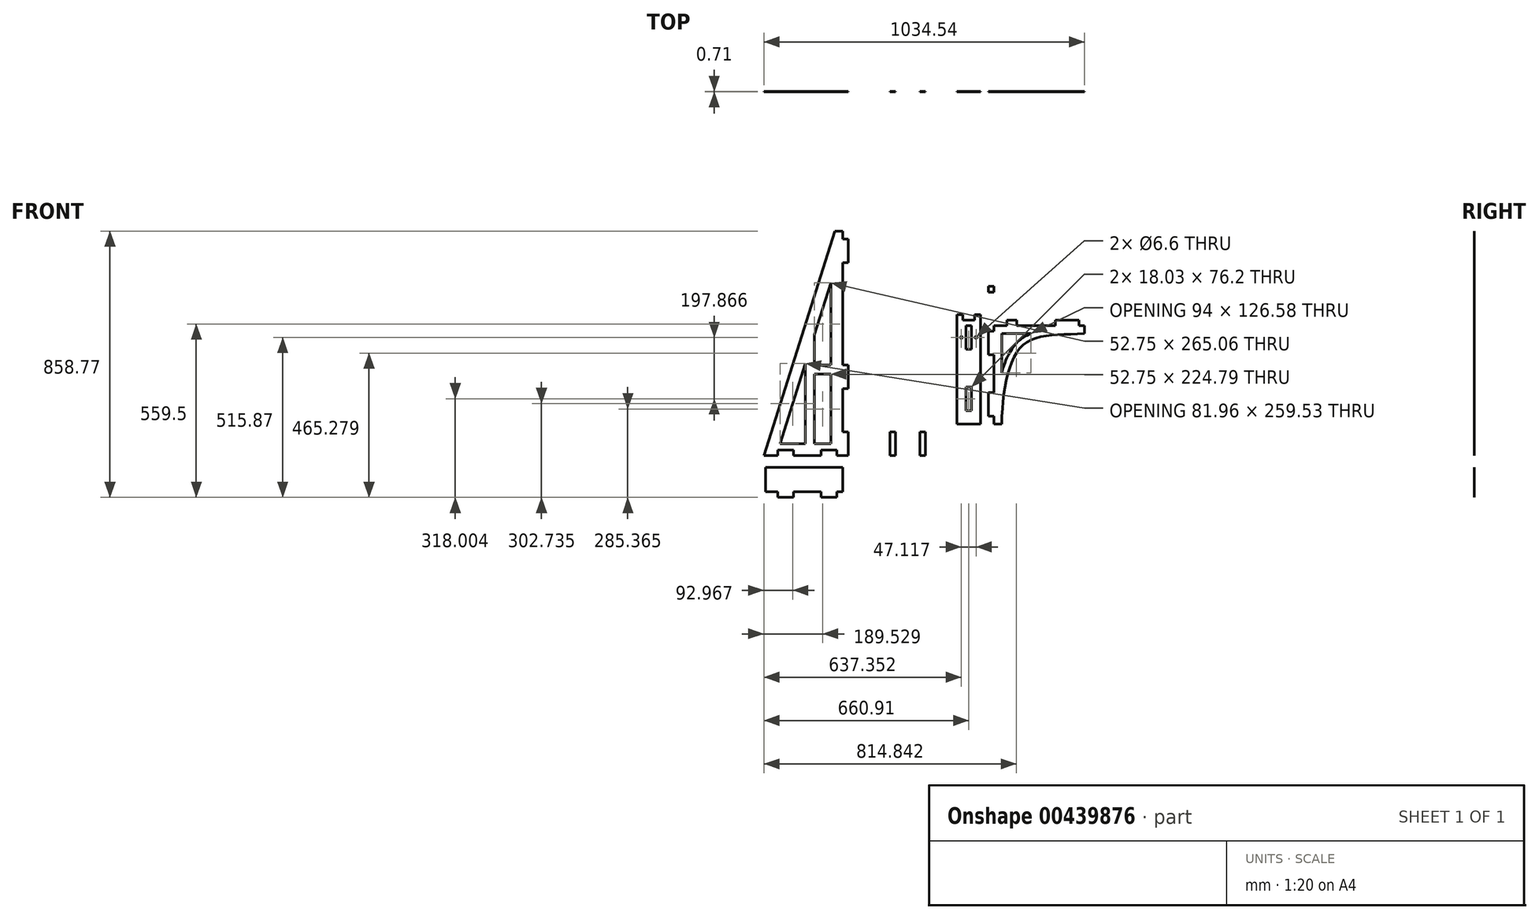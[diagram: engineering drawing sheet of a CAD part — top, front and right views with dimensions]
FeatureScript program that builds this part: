
annotation { "Feature Type Name" : "Feature", "Feature Type Description" : "" }
export const myFeature = defineFeature(function(context is Context, id is Id, definition is map)
    precondition{}
    {
        {
            assignVariable(context, id + "F0", {"name" : "ply34", "anyValue" : .71});
        }
        {
            var Q0;
            Q0=qCreatedBy(makeId("Front.planeOp"),FACE);
            var sketch = newSketch(context, id + "F1", { "sketchPlane" : qUnion([Q0])});
            skLineSegment(sketch, "E0.bottom", {"start": v(-508, 38.1) * mm, "end": v(508, 38.1) * mm});
            skLineSegment(sketch, "E0.top", {"start": v(-508, -38.1) * mm, "end": v(508, -38.1) * mm});
            skLineSegment(sketch, "E0.left", {"start": v(-508, 38.1) * mm, "end": v(-508, -38.1) * mm});
            skLineSegment(sketch, "E0.right", {"start": v(508, 38.1) * mm, "end": v(508, -38.1) * mm});
            skPoint(sketch, "E0.middle", {"position": v(0, 0) * mm});
            skLineSegment(sketch, "E1", {"start": v(0, 0) * mm, "end": v(-152.4, 0) * mm});
            skLineSegment(sketch, "E2", {"start": v(-152.4, 0) * mm, "end": v(0, 0) * mm});
            skLineSegment(sketch, "E3", {"start": v(0, 0) * mm, "end": v(152.4, 0) * mm});
            skArc(sketch, "E4.0.startCap", {"start": v(-152.4, -3.3) * mm, "mid": v(-155.7, 0) * mm, "end": v(-152.4, 3.3) * mm});
            skArc(sketch, "E4.0.endCap", {"start": v(0, 3.3) * mm, "mid": v(3.3, 0) * mm, "end": v(0, -3.3) * mm});
            skLineSegment(sketch, "E4.0.left", {"start": v(-152.4, 3.3) * mm, "end": v(0, 3.3) * mm});
            skLineSegment(sketch, "E4.0.right", {"start": v(-152.4, -3.3) * mm, "end": v(0, -3.3) * mm});
            skArc(sketch, "E4.1.startCap", {"start": v(0, -3.3) * mm, "mid": v(-3.3, 0) * mm, "end": v(0, 3.3) * mm});
            skArc(sketch, "E4.1.endCap", {"start": v(152.4, 3.3) * mm, "mid": v(155.7, 0) * mm, "end": v(152.4, -3.3) * mm});
            skLineSegment(sketch, "E4.1.left", {"start": v(0, 3.3) * mm, "end": v(152.4, 3.3) * mm});
            skLineSegment(sketch, "E4.1.right", {"start": v(0, -3.3) * mm, "end": v(152.4, -3.3) * mm});
            skLineSegment(sketch, "E5.bottom", {"start": v(-292.1, 9.02) * mm, "end": v(-215.9, 9.02) * mm});
            skLineSegment(sketch, "E5.top", {"start": v(-292.1, -9.02) * mm, "end": v(-215.9, -9.02) * mm});
            skLineSegment(sketch, "E5.left", {"start": v(-292.1, 9.02) * mm, "end": v(-292.1, -9.02) * mm});
            skLineSegment(sketch, "E5.right", {"start": v(-215.9, 9.02) * mm, "end": v(-215.9, -9.02) * mm});
            skPoint(sketch, "E5.middle", {"position": v(-254, 0) * mm});
            skLineSegment(sketch, "E6.bottom", {"start": v(-415.93, 9.02) * mm, "end": v(-447.68, 9.02) * mm});
            skLineSegment(sketch, "E6.top", {"start": v(-415.93, -9.02) * mm, "end": v(-447.68, -9.02) * mm});
            skLineSegment(sketch, "E6.left", {"start": v(-415.93, 9.02) * mm, "end": v(-415.93, -9.02) * mm});
            skLineSegment(sketch, "E6.right", {"start": v(-447.68, 9.02) * mm, "end": v(-447.68, -9.02) * mm});
            skPoint(sketch, "E6.middle", {"position": v(-431.8, 0) * mm});
            skPoint(sketch, "E6.middle.positionSnap0", {"position": v(-292.1, 0) * mm});
            skPoint(sketch, "E6.centerSnap0", {"position": v(-292.1, 0) * mm});
            skLineSegment(sketch, "E7.bottom", {"start": v(-508, 38.1) * mm, "end": v(-489.97, 38.1) * mm});
            skLineSegment(sketch, "E7.top", {"start": v(-508, 19.05) * mm, "end": v(-489.97, 19.05) * mm});
            skLineSegment(sketch, "E7.left", {"start": v(-508, 38.1) * mm, "end": v(-508, 19.05) * mm});
            skLineSegment(sketch, "E7.right", {"start": v(-489.97, 38.1) * mm, "end": v(-489.97, 19.05) * mm});
            skLineSegment(sketch, "E8.bottom", {"start": v(-508, -38.1) * mm, "end": v(-489.97, -38.1) * mm});
            skLineSegment(sketch, "E8.top", {"start": v(-508, -19.05) * mm, "end": v(-489.97, -19.05) * mm});
            skLineSegment(sketch, "E8.left", {"start": v(-508, -38.1) * mm, "end": v(-508, -19.05) * mm});
            skLineSegment(sketch, "E8.right", {"start": v(-489.97, -38.1) * mm, "end": v(-489.97, -19.05) * mm});
            skLineSegment(sketch, "E9", {"start": v(-489.97, -88.9) * mm, "end": v(-197.87, -88.9) * mm});
            skLineSegment(sketch, "E10", {"start": v(-197.87, -88.9) * mm, "end": v(-197.87, -114.3) * mm});
            skLineSegment(sketch, "E11", {"start": v(-489.97, -88.9) * mm, "end": v(-489.97, -381) * mm});
            skLineSegment(sketch, "E12", {"start": v(-489.97, -381) * mm, "end": v(-464.57, -381) * mm, "construction": true});
            skFitSpline(sketch, "E13", {"points": [v(-197.87, -114.3) * mm, v(-396.07, -151.38) * mm, v(-464.57, -381) * mm], "startDerivative": vector(-532.47, -33.14) * mm, "endDerivative": vector(-35.57, -553.13) * mm});
            skFitSpline(sketch, "E14.0", {"points": [v(-199.05, -95.29) * mm, v(-209.95, -95.96) * mm, v(-231.35, -96.96) * mm, v(-262.2, -98.06) * mm, v(-291.7, -99.5) * mm, v(-315.11, -101.64) * mm, v(-333.14, -104.34) * mm, v(-346.3, -106.98) * mm, v(-359.07, -110.37) * mm, v(-371.45, -114.64) * mm, v(-383.38, -119.94) * mm, v(-392.88, -125.32) * mm, v(-400.15, -130.26) * mm, v(-404.55, -133.62) * mm, v(-407.97, -136.47) * mm, v(-411.32, -139.43) * mm, v(-415.36, -143.3) * mm, v(-419.95, -148.22) * mm, v(-425.77, -155.12) * mm, v(-432.47, -164.32) * mm, v(-439.67, -176.21) * mm, v(-448.25, -193.08) * mm, v(-457.24, -215.9) * mm, v(-465.75, -245.64) * mm, v(-472.36, -277.33) * mm, v(-477.36, -310.53) * mm, v(-481.06, -344.83) * mm, v(-482.83, -368.1) * mm, v(-483.58, -379.78) * mm]});
            skLineSegment(sketch, "E15.0", {"start": v(-464.57, -114.3) * mm, "end": v(-370.05, -114.3) * mm});
            skLineSegment(sketch, "E15.1", {"start": v(-464.57, -114.3) * mm, "end": v(-464.57, -242.5) * mm});
            skLineSegment(sketch, "E16", {"start": v(-292.1, -88.9) * mm, "end": v(-292.1, -70.87) * mm});
            skLineSegment(sketch, "E17", {"start": v(-292.1, -70.87) * mm, "end": v(-215.9, -70.87) * mm});
            skLineSegment(sketch, "E18", {"start": v(-215.9, -70.87) * mm, "end": v(-215.9, -88.9) * mm});
            skLineSegment(sketch, "E19", {"start": v(-447.68, -88.9) * mm, "end": v(-447.68, -70.87) * mm});
            skLineSegment(sketch, "E20", {"start": v(-447.68, -70.87) * mm, "end": v(-415.93, -70.87) * mm});
            skLineSegment(sketch, "E21", {"start": v(-415.93, -70.87) * mm, "end": v(-415.93, -88.9) * mm});
            skLineSegment(sketch, "E22", {"start": v(-489.97, -381) * mm, "end": v(-508, -381) * mm});
            skLineSegment(sketch, "E23", {"start": v(-508, -381) * mm, "end": v(-508, -304.8) * mm});
            skLineSegment(sketch, "E24", {"start": v(-508, -304.8) * mm, "end": v(-489.97, -304.8) * mm});
            skLineSegment(sketch, "E25.bottom", {"start": v(-533.4, -70.87) * mm, "end": v(-609.6, -70.87) * mm});
            skLineSegment(sketch, "E25.top", {"start": v(-533.4, -406.4) * mm, "end": v(-609.6, -406.4) * mm});
            skLineSegment(sketch, "E25.left", {"start": v(-533.4, -70.87) * mm, "end": v(-533.4, -406.4) * mm});
            skLineSegment(sketch, "E25.right", {"start": v(-609.6, -70.87) * mm, "end": v(-609.6, -406.4) * mm});
            skLineSegment(sketch, "E26", {"start": v(-609.6, -70.87) * mm, "end": v(-609.6, -52.83) * mm});
            skLineSegment(sketch, "E27", {"start": v(-609.6, -52.83) * mm, "end": v(-590.55, -52.83) * mm});
            skLineSegment(sketch, "E28", {"start": v(-590.55, -52.83) * mm, "end": v(-590.55, -70.87) * mm});
            skLineSegment(sketch, "E29", {"start": v(-533.4, -70.87) * mm, "end": v(-533.4, -52.83) * mm});
            skLineSegment(sketch, "E30", {"start": v(-533.4, -52.83) * mm, "end": v(-552.45, -52.83) * mm});
            skLineSegment(sketch, "E31", {"start": v(-552.45, -52.83) * mm, "end": v(-552.45, -70.87) * mm});
            skLineSegment(sketch, "E32.bottom", {"start": v(-562.48, -88.9) * mm, "end": v(-580.52, -88.9) * mm});
            skLineSegment(sketch, "E32.top", {"start": v(-562.48, -165.1) * mm, "end": v(-580.52, -165.1) * mm});
            skLineSegment(sketch, "E32.left", {"start": v(-562.48, -88.9) * mm, "end": v(-562.48, -165.1) * mm});
            skLineSegment(sketch, "E32.right", {"start": v(-580.52, -88.9) * mm, "end": v(-580.52, -165.1) * mm});
            skPoint(sketch, "E32.middle", {"position": v(-571.5, -127) * mm});
            skPoint(sketch, "E32.middle.positionSnap1", {"position": v(-571.5, -70.87) * mm});
            skPoint(sketch, "E32.centerSnap1", {"position": v(-571.5, -70.87) * mm});
            skPoint(sketch, "E33.middle.positionSnap0", {"position": v(-571.5, -406.4) * mm});
            skPoint(sketch, "E33.middle.positionSnap1", {"position": v(-508, -342.9) * mm});
            skPoint(sketch, "E33.centerSnap0", {"position": v(-571.5, -406.4) * mm});
            skPoint(sketch, "E33.centerSnap1", {"position": v(-508, -342.9) * mm});
            skLineSegment(sketch, "E34.top", {"start": v(-489.97, -406.4) * mm, "end": v(-464.57, -406.4) * mm});
            skLineSegment(sketch, "E34.left", {"start": v(-489.97, -381) * mm, "end": v(-489.97, -406.4) * mm});
            skLineSegment(sketch, "E34.right", {"start": v(-464.57, -381) * mm, "end": v(-464.57, -406.4) * mm});
            skLineSegment(sketch, "E35", {"start": v(-580.52, -127) * mm, "end": v(-609.6, -127) * mm, "construction": true});
            skCircle(sketch, "E36", {"center": v(-595.06, -127) * mm, "radius": 3.3 * mm});
            skLineSegment(sketch, "E37", {"start": v(-562.48, -127) * mm, "end": v(-533.4, -127) * mm, "construction": true});
            skCircle(sketch, "E38", {"center": v(-547.94, -127) * mm, "radius": 3.3 * mm});
            skLineSegment(sketch, "E39.bottom", {"start": v(-826, 406.4) * mm, "end": v(-711.2, 406.4) * mm});
            skLineSegment(sketch, "E39.top", {"start": v(-826, -508) * mm, "end": v(-711.2, -508) * mm});
            skLineSegment(sketch, "E39.left", {"start": v(-826, 406.4) * mm, "end": v(-826, -508) * mm});
            skLineSegment(sketch, "E39.right", {"start": v(-711.2, 406.4) * mm, "end": v(-711.2, -508) * mm});
            skLineSegment(sketch, "E40.bottom", {"start": v(-711.2, -508) * mm, "end": v(-729.23, -508) * mm});
            skLineSegment(sketch, "E40.top", {"start": v(-711.2, -431.8) * mm, "end": v(-729.23, -431.8) * mm});
            skLineSegment(sketch, "E40.left", {"start": v(-711.2, -508) * mm, "end": v(-711.2, -431.8) * mm});
            skLineSegment(sketch, "E40.right", {"start": v(-729.23, -508) * mm, "end": v(-729.23, -431.8) * mm});
            skLineSegment(sketch, "E41.bottom", {"start": v(-711.2, 406.4) * mm, "end": v(-729.23, 406.4) * mm, "construction": true});
            skLineSegment(sketch, "E41.top", {"start": v(-711.2, 355.6) * mm, "end": v(-729.23, 355.6) * mm, "construction": true});
            skLineSegment(sketch, "E41.left", {"start": v(-711.2, 406.4) * mm, "end": v(-711.2, 355.6) * mm, "construction": true});
            skLineSegment(sketch, "E41.right", {"start": v(-729.23, 406.4) * mm, "end": v(-729.23, 355.6) * mm, "construction": true});
            skLineSegment(sketch, "E42", {"start": v(-768.6, 406.4) * mm, "end": v(-768.6, -508) * mm, "construction": true});
            skLineSegment(sketch, "E43.MirrorCS", {"start": v(-826, 406.4) * mm, "end": v(-807.97, 406.4) * mm, "construction": true});
            skLineSegment(sketch, "E44.MirrorCS", {"start": v(-826, 406.4) * mm, "end": v(-826, 355.6) * mm, "construction": true});
            skLineSegment(sketch, "E45.MirrorCS", {"start": v(-807.97, 406.4) * mm, "end": v(-807.97, 355.6) * mm, "construction": true});
            skLineSegment(sketch, "E46.MirrorCS", {"start": v(-826, 355.6) * mm, "end": v(-807.97, 355.6) * mm, "construction": true});
            skLineSegment(sketch, "E47.MirrorCS", {"start": v(-807.97, -508) * mm, "end": v(-807.97, -431.8) * mm});
            skLineSegment(sketch, "E48.MirrorCS", {"start": v(-826, -431.8) * mm, "end": v(-807.97, -431.8) * mm});
            skLineSegment(sketch, "E49.MirrorCS", {"start": v(-826, -508) * mm, "end": v(-826, -431.8) * mm});
            skLineSegment(sketch, "E50.MirrorCS", {"start": v(-826, -508) * mm, "end": v(-807.97, -508) * mm});
            skLineSegment(sketch, "E51.bottom", {"start": v(-711.2, -215.9) * mm, "end": v(-729.23, -215.9) * mm});
            skLineSegment(sketch, "E51.top", {"start": v(-711.2, -292.1) * mm, "end": v(-729.23, -292.1) * mm});
            skLineSegment(sketch, "E51.left", {"start": v(-711.2, -215.9) * mm, "end": v(-711.2, -292.1) * mm});
            skLineSegment(sketch, "E51.right", {"start": v(-729.23, -215.9) * mm, "end": v(-729.23, -292.1) * mm});
            skLineSegment(sketch, "E52.bottom", {"start": v(-711.2, 190.5) * mm, "end": v(-729.23, 190.5) * mm});
            skLineSegment(sketch, "E52.top", {"start": v(-711.2, 114.3) * mm, "end": v(-729.23, 114.3) * mm});
            skLineSegment(sketch, "E52.left", {"start": v(-711.2, 190.5) * mm, "end": v(-711.2, 114.3) * mm});
            skLineSegment(sketch, "E52.right", {"start": v(-729.23, 190.5) * mm, "end": v(-729.23, 114.3) * mm});
            skLineSegment(sketch, "E53.MirrorCS", {"start": v(-826, -215.9) * mm, "end": v(-807.97, -215.9) * mm});
            skLineSegment(sketch, "E54.MirrorCS", {"start": v(-826, -292.1) * mm, "end": v(-807.97, -292.1) * mm});
            skLineSegment(sketch, "E55.MirrorCS", {"start": v(-826, 190.5) * mm, "end": v(-807.97, 190.5) * mm});
            skLineSegment(sketch, "E56.MirrorCS", {"start": v(-826, 114.3) * mm, "end": v(-807.97, 114.3) * mm});
            skLineSegment(sketch, "E57.MirrorCS", {"start": v(-807.97, 190.5) * mm, "end": v(-807.97, 114.3) * mm});
            skLineSegment(sketch, "E58.MirrorCS", {"start": v(-826, 190.5) * mm, "end": v(-826, 114.3) * mm});
            skLineSegment(sketch, "E59.MirrorCS", {"start": v(-807.97, -215.9) * mm, "end": v(-807.97, -292.1) * mm});
            skLineSegment(sketch, "E60.MirrorCS", {"start": v(-826, -215.9) * mm, "end": v(-826, -292.1) * mm});
            skLineSegment(sketch, "E61", {"start": v(-595.06, -127) * mm, "end": v(-547.94, -127) * mm, "construction": true});
            skLineSegment(sketch, "E62", {"start": v(-792.16, -50.8) * mm, "end": v(-745.05, -50.8) * mm, "construction": true});
            skPoint(sketch, "E62.startSnap0", {"position": v(-768.6, -50.8) * mm});
            skLineSegment(sketch, "E63", {"start": v(-792.16, 76.2) * mm, "end": v(-792.16, -177.8) * mm, "construction": true});
            skLineSegment(sketch, "E64", {"start": v(-745.05, 76.2) * mm, "end": v(-745.05, -177.8) * mm, "construction": true});
            skArc(sketch, "E65.0.startCap", {"start": v(-795.46, 76.2) * mm, "mid": v(-792.16, 79.5) * mm, "end": v(-788.86, 76.2) * mm});
            skArc(sketch, "E65.0.endCap", {"start": v(-788.86, -177.8) * mm, "mid": v(-792.16, -181.1) * mm, "end": v(-795.46, -177.8) * mm});
            skLineSegment(sketch, "E65.0.left", {"start": v(-788.86, 76.2) * mm, "end": v(-788.86, -177.8) * mm});
            skLineSegment(sketch, "E65.0.right", {"start": v(-795.46, 76.2) * mm, "end": v(-795.46, -177.8) * mm});
            skArc(sketch, "E66.0.startCap", {"start": v(-748.35, 76.2) * mm, "mid": v(-745.05, 79.5) * mm, "end": v(-741.74, 76.2) * mm});
            skArc(sketch, "E66.0.endCap", {"start": v(-741.74, -177.8) * mm, "mid": v(-745.05, -181.1) * mm, "end": v(-748.35, -177.8) * mm});
            skLineSegment(sketch, "E66.0.left", {"start": v(-741.74, 76.2) * mm, "end": v(-741.74, -177.8) * mm});
            skLineSegment(sketch, "E66.0.right", {"start": v(-748.35, 76.2) * mm, "end": v(-748.35, -177.8) * mm});
            skLineSegment(sketch, "E67", {"start": v(-978.4, 215.9) * mm, "end": v(-978.4, -508) * mm});
            skLineSegment(sketch, "E68", {"start": v(-978.4, -508) * mm, "end": v(-1232.4, -508) * mm});
            skLineSegment(sketch, "E69", {"start": v(-1232.4, -508) * mm, "end": v(-1003.8, 215.9) * mm});
            skLineSegment(sketch, "E70", {"start": v(-1003.8, 215.9) * mm, "end": v(-978.4, 215.9) * mm});
            skLineSegment(sketch, "E71", {"start": v(-978.4, 190.5) * mm, "end": v(-960.37, 190.5) * mm});
            skLineSegment(sketch, "E72", {"start": v(-960.37, 190.5) * mm, "end": v(-960.37, 114.3) * mm});
            skLineSegment(sketch, "E73", {"start": v(-960.37, 114.3) * mm, "end": v(-978.4, 114.3) * mm});
            skLineSegment(sketch, "E74", {"start": v(-978.4, -215.9) * mm, "end": v(-960.37, -215.9) * mm});
            skLineSegment(sketch, "E75", {"start": v(-960.37, -215.9) * mm, "end": v(-960.37, -292.1) * mm});
            skLineSegment(sketch, "E76", {"start": v(-960.37, -292.1) * mm, "end": v(-978.4, -292.1) * mm});
            skLineSegment(sketch, "E77", {"start": v(-978.4, -508) * mm, "end": v(-960.37, -508) * mm});
            skLineSegment(sketch, "E78", {"start": v(-960.37, -508) * mm, "end": v(-960.37, -431.8) * mm});
            skLineSegment(sketch, "E79", {"start": v(-960.37, -431.8) * mm, "end": v(-978.4, -431.8) * mm});
            skLineSegment(sketch, "E80.0", {"start": v(-1016.5, 49.16) * mm, "end": v(-1016.5, -215.9) * mm});
            skLineSegment(sketch, "E80.1", {"start": v(-1180.42, -469.9) * mm, "end": v(-1098.46, -210.37) * mm});
            skLineSegment(sketch, "E80.2", {"start": v(-1016.5, -469.9) * mm, "end": v(-1069.25, -469.9) * mm});
            skLineSegment(sketch, "E81", {"start": v(-1098.46, -469.9) * mm, "end": v(-1098.46, -210.37) * mm});
            skLineSegment(sketch, "E82", {"start": v(-1069.25, -469.9) * mm, "end": v(-1069.25, -245.11) * mm});
            skLineSegment(sketch, "E83.trimOffspring", {"start": v(-1069.25, -117.87) * mm, "end": v(-1016.5, 49.16) * mm});
            skLineSegment(sketch, "E84.trimOffspring", {"start": v(-1098.46, -469.9) * mm, "end": v(-1180.42, -469.9) * mm});
            skLineSegment(sketch, "E85", {"start": v(-1016.5, -215.9) * mm, "end": v(-1069.25, -215.9) * mm});
            skLineSegment(sketch, "E86", {"start": v(-1069.25, -245.11) * mm, "end": v(-1016.5, -245.11) * mm});
            skLineSegment(sketch, "E87.trimOffspring", {"start": v(-1016.5, -245.11) * mm, "end": v(-1016.5, -469.9) * mm});
            skLineSegment(sketch, "E88.trimOffspring", {"start": v(-1069.25, -215.9) * mm, "end": v(-1069.25, -117.87) * mm});
            skLineSegment(sketch, "E89", {"start": v(-997.46, -508) * mm, "end": v(-997.46, -489.97) * mm});
            skLineSegment(sketch, "E90", {"start": v(-997.46, -489.97) * mm, "end": v(-1048.26, -489.97) * mm});
            skLineSegment(sketch, "E91", {"start": v(-1048.26, -489.97) * mm, "end": v(-1048.26, -508) * mm});
            skLineSegment(sketch, "E92", {"start": v(-1048.26, -508) * mm, "end": v(-997.46, -508) * mm});
            skLineSegment(sketch, "E93.bottom", {"start": v(-1137.16, -508) * mm, "end": v(-1187.96, -508) * mm});
            skLineSegment(sketch, "E93.top", {"start": v(-1137.16, -489.97) * mm, "end": v(-1187.96, -489.97) * mm});
            skLineSegment(sketch, "E93.left", {"start": v(-1137.16, -508) * mm, "end": v(-1137.16, -489.97) * mm});
            skLineSegment(sketch, "E93.right", {"start": v(-1187.96, -508) * mm, "end": v(-1187.96, -489.97) * mm});
            skLineSegment(sketch, "E94", {"start": v(-1226.71, -489.97) * mm, "end": v(-1226.71, -508) * mm, "construction": true});
            skLineSegment(sketch, "E95.bottom", {"start": v(-1226.71, -546.1) * mm, "end": v(-978.4, -546.1) * mm});
            skLineSegment(sketch, "E95.top", {"start": v(-1226.71, -624.84) * mm, "end": v(-978.4, -624.84) * mm});
            skLineSegment(sketch, "E95.left", {"start": v(-1226.71, -546.1) * mm, "end": v(-1226.71, -624.84) * mm});
            skLineSegment(sketch, "E95.right", {"start": v(-978.4, -546.1) * mm, "end": v(-978.4, -624.84) * mm});
            skLineSegment(sketch, "E96", {"start": v(-807.97, -469.9) * mm, "end": v(-729.23, -469.9) * mm, "construction": true});
            skLineSegment(sketch, "E97.bottom", {"start": v(-1187.96, -546.1) * mm, "end": v(-1137.16, -546.1) * mm});
            skLineSegment(sketch, "E97.top", {"start": v(-1187.96, -528.07) * mm, "end": v(-1137.16, -528.07) * mm});
            skLineSegment(sketch, "E97.left", {"start": v(-1187.96, -546.1) * mm, "end": v(-1187.96, -528.07) * mm});
            skLineSegment(sketch, "E97.right", {"start": v(-1137.16, -546.1) * mm, "end": v(-1137.16, -528.07) * mm});
            skLineSegment(sketch, "E98.bottom", {"start": v(-997.46, -546.1) * mm, "end": v(-1048.26, -546.1) * mm});
            skLineSegment(sketch, "E98.top", {"start": v(-997.46, -528.07) * mm, "end": v(-1048.26, -528.07) * mm});
            skLineSegment(sketch, "E98.left", {"start": v(-997.46, -546.1) * mm, "end": v(-997.46, -528.07) * mm});
            skLineSegment(sketch, "E98.right", {"start": v(-1048.26, -546.1) * mm, "end": v(-1048.26, -528.07) * mm});
            skLineSegment(sketch, "E99", {"start": v(-1226.71, -585.47) * mm, "end": v(-978.4, -585.47) * mm, "construction": true});
            skLineSegment(sketch, "E100.MirrorCS", {"start": v(-1187.96, -642.87) * mm, "end": v(-1137.16, -642.87) * mm});
            skLineSegment(sketch, "E101.MirrorCS", {"start": v(-1187.96, -624.84) * mm, "end": v(-1137.16, -624.84) * mm});
            skLineSegment(sketch, "E102.MirrorCS", {"start": v(-1187.96, -624.84) * mm, "end": v(-1187.96, -642.87) * mm});
            skLineSegment(sketch, "E103.MirrorCS", {"start": v(-997.46, -642.87) * mm, "end": v(-1048.26, -642.87) * mm});
            skLineSegment(sketch, "E104.MirrorCS", {"start": v(-1137.16, -624.84) * mm, "end": v(-1137.16, -642.87) * mm});
            skLineSegment(sketch, "E105.MirrorCS", {"start": v(-997.46, -624.84) * mm, "end": v(-997.46, -642.87) * mm});
            skLineSegment(sketch, "E106.MirrorCS", {"start": v(-1048.26, -624.84) * mm, "end": v(-1048.26, -642.87) * mm});
            skLineSegment(sketch, "E107.MirrorCS", {"start": v(-997.46, -624.84) * mm, "end": v(-1048.26, -624.84) * mm});
            skLineSegment(sketch, "E108.bottom", {"start": v(-489.97, -106.93) * mm, "end": v(-508, -106.93) * mm});
            skLineSegment(sketch, "E108.top", {"start": v(-489.97, -183.13) * mm, "end": v(-508, -183.13) * mm});
            skLineSegment(sketch, "E108.left", {"start": v(-489.97, -106.93) * mm, "end": v(-489.97, -183.13) * mm});
            skLineSegment(sketch, "E108.right", {"start": v(-508, -106.93) * mm, "end": v(-508, -183.13) * mm});
            skLineSegment(sketch, "E109.bottom", {"start": v(-562.48, -362.97) * mm, "end": v(-580.52, -362.97) * mm});
            skLineSegment(sketch, "E109.top", {"start": v(-562.48, -286.77) * mm, "end": v(-580.52, -286.77) * mm});
            skLineSegment(sketch, "E109.left", {"start": v(-562.48, -362.97) * mm, "end": v(-562.48, -286.77) * mm});
            skLineSegment(sketch, "E109.right", {"start": v(-580.52, -362.97) * mm, "end": v(-580.52, -286.77) * mm});
            skPoint(sketch, "E109.middle", {"position": v(-571.5, -324.87) * mm});
            skLineSegment(sketch, "E110", {"start": v(-508, -183.13) * mm, "end": v(-508, -304.8) * mm, "construction": true});
            skLineSegment(sketch, "E111", {"start": v(-562.48, -165.1) * mm, "end": v(-562.48, -286.77) * mm, "construction": true});
            skLineSegment(sketch, "E112", {"start": v(-768.6, 406.4) * mm, "end": v(-768.6, 381) * mm});
            skArc(sketch, "E113.0.startCap", {"start": v(-771.9, 406.4) * mm, "mid": v(-768.6, 409.7) * mm, "end": v(-765.3, 406.4) * mm});
            skArc(sketch, "E113.0.endCap", {"start": v(-765.3, 381) * mm, "mid": v(-768.6, 377.7) * mm, "end": v(-771.9, 381) * mm});
            skLineSegment(sketch, "E113.0.left", {"start": v(-765.3, 406.4) * mm, "end": v(-765.3, 381) * mm});
            skLineSegment(sketch, "E113.0.right", {"start": v(-771.9, 406.4) * mm, "end": v(-771.9, 381) * mm});
            skLineSegment(sketch, "E114", {"start": v(508, 0) * mm, "end": v(469.9, 0) * mm, "construction": true});
            skLineSegment(sketch, "E115", {"start": v(469.9, 15.87) * mm, "end": v(469.9, -15.87) * mm, "construction": true});
            skCircle(sketch, "E116", {"center": v(469.9, 15.87) * mm, "radius": 9.53 * mm});
            skCircle(sketch, "E117", {"center": v(469.9, -15.87) * mm, "radius": 9.53 * mm});
            skSolve(sketch);
        }
        {
            var Q0;
            {var subQ14=sQuery(id+"F1.wireOp",EDGE,"E69");Q0=makeQuery(id+"F1.imprint","IMPRINT",FACE,{"disambiguationData":[TD([[makeQuery(id+"F1.imprint","IMPRINT",EDGE,{"derivedFrom":subQ14}),-1.0]])]});}
            var Q1;
            {var subQ0=sQuery(id+"F1.wireOp",EDGE,"E71");Q1=makeQuery(id+"F1.imprint","IMPRINT",FACE,{"disambiguationData":[TD([[makeQuery(id+"F1.imprint","IMPRINT",EDGE,{"derivedFrom":subQ0}),-1.0]])]});}
            var Q2;
            {var subQ0=sQuery(id+"F1.wireOp",EDGE,"E74");Q2=makeQuery(id+"F1.imprint","IMPRINT",FACE,{"disambiguationData":[TD([[makeQuery(id+"F1.imprint","IMPRINT",EDGE,{"derivedFrom":subQ0}),-1.0]])]});}
            var Q3;
            {var subQ0=sQuery(id+"F1.wireOp",EDGE,"E77");Q3=makeQuery(id+"F1.imprint","IMPRINT",FACE,{"disambiguationData":[TD([[makeQuery(id+"F1.imprint","IMPRINT",EDGE,{"derivedFrom":subQ0}),1.0]])]});}
            var Q4;
            Q4=makeQuery(id+"F1.imprint","IMPRINT",FACE,{"disambiguationData":[TD([[makeQuery(id+"F1.imprint","IMPRINT",EDGE,{"derivedFrom":sQuery(id+"F1.wireOp",EDGE,"E98.bottom")}),-1.0]])]});
            var Q5;
            Q5=makeQuery(id+"F1.imprint","IMPRINT",FACE,{"disambiguationData":[TD([[makeQuery(id+"F1.imprint","IMPRINT",EDGE,{"derivedFrom":sQuery(id+"F1.wireOp",EDGE,"E97.bottom")}),1.0]])]});
            var Q6;
            {var subQ2=sQuery(id+"F1.wireOp",EDGE,"E95.left");Q6=makeQuery(id+"F1.imprint","IMPRINT",FACE,{"disambiguationData":[TD([[makeQuery(id+"F1.imprint","IMPRINT",EDGE,{"derivedFrom":subQ2}),1.0]])]});}
            var Q7;
            Q7=makeQuery(id+"F1.imprint","IMPRINT",FACE,{"disambiguationData":[TD([[makeQuery(id+"F1.imprint","IMPRINT",EDGE,{"derivedFrom":sQuery(id+"F1.wireOp",EDGE,"E103.MirrorCS")}),-1.0]])]});
            var Q8;
            Q8=makeQuery(id+"F1.imprint","IMPRINT",FACE,{"disambiguationData":[TD([[makeQuery(id+"F1.imprint","IMPRINT",EDGE,{"derivedFrom":sQuery(id+"F1.wireOp",EDGE,"E0.bottom")}),-1.0]])]});
            var Q9;
            {var subQ6=sQuery(id+"F1.wireOp",EDGE,"E10");Q9=makeQuery(id+"F1.imprint","IMPRINT",FACE,{"disambiguationData":[TD([[makeQuery(id+"F1.imprint","IMPRINT",EDGE,{"derivedFrom":subQ6}),-1.0]])]});}
            var Q10;
            {var subQ0=sQuery(id+"F1.wireOp",EDGE,"E16");Q10=makeQuery(id+"F1.imprint","IMPRINT",FACE,{"disambiguationData":[TD([[makeQuery(id+"F1.imprint","IMPRINT",EDGE,{"derivedFrom":subQ0}),-1.0]])]});}
            var Q11;
            {var subQ0=sQuery(id+"F1.wireOp",EDGE,"E19");Q11=makeQuery(id+"F1.imprint","IMPRINT",FACE,{"disambiguationData":[TD([[makeQuery(id+"F1.imprint","IMPRINT",EDGE,{"derivedFrom":subQ0}),-1.0]])]});}
            var Q12;
            {var subQ0=sQuery(id+"F1.wireOp",EDGE,"XXwvfhwP-Kl7B-pzMR-Daqk-7tzTg0mTjpYv");Q12=makeQuery(id+"F1.imprint","IMPRINT",FACE,{"disambiguationData":[TD([[makeQuery(id+"F1.imprint","IMPRINT",EDGE,{"derivedFrom":subQ0}),1.0]])]});}
            var Q13;
            {var subQ0=sQuery(id+"F1.wireOp",EDGE,"E29");Q13=makeQuery(id+"F1.imprint","IMPRINT",FACE,{"disambiguationData":[TD([[makeQuery(id+"F1.imprint","IMPRINT",EDGE,{"derivedFrom":subQ0}),1.0]])]});}
            var Q14;
            {var subQ0=sQuery(id+"F1.wireOp",EDGE,"E26");Q14=makeQuery(id+"F1.imprint","IMPRINT",FACE,{"disambiguationData":[TD([[makeQuery(id+"F1.imprint","IMPRINT",EDGE,{"derivedFrom":subQ0}),-1.0]])]});}
            var Q15;
            Q15=makeQuery(id+"F1.imprint","IMPRINT",FACE,{"disambiguationData":[TD([[makeQuery(id+"F1.imprint","IMPRINT",EDGE,{"derivedFrom":sQuery(id+"F1.wireOp",EDGE,"E25.top")}),-1.0]])]});
            var Q16;
            {var subQ0=sQuery(id+"F1.wireOp",EDGE,"E22");Q16=makeQuery(id+"F1.imprint","IMPRINT",FACE,{"disambiguationData":[TD([[makeQuery(id+"F1.imprint","IMPRINT",EDGE,{"derivedFrom":subQ0}),-1.0]])]});}
            var Q17;
            Q17=makeQuery(id+"F1.imprint","IMPRINT",FACE,{"disambiguationData":[TD([[makeQuery(id+"F1.imprint","IMPRINT",EDGE,{"derivedFrom":sQuery(id+"F1.wireOp",EDGE,"E108.bottom")}),1.0]])]});
            var Q18;
            Q18=makeQuery(id+"F1.imprint","IMPRINT",FACE,{"disambiguationData":[TD([[makeQuery(id+"F1.imprint","IMPRINT",EDGE,{"derivedFrom":sQuery(id+"F1.wireOp",EDGE,"E100.MirrorCS")}),1.0]])]});
            var Q19;
            Q19=makeQuery(id+"F1.imprint","IMPRINT",FACE,{"disambiguationData":[TD([[makeQuery(id+"F1.imprint","IMPRINT",EDGE,{"derivedFrom":sQuery(id+"F1.wireOp",EDGE,"E39.top")}),1.0]])]});
            extrude(context, id + "F2", {"entities" : qUnion([Q0, Q1, Q2, Q3, Q4, Q5, Q6, Q7, Q8, Q9, Q10, Q11, Q12, Q13, Q14, Q15, Q16, Q17, Q18, Q19]), "depth" : (getVariable(context, 'ply34')) * mm});
        }
    });
